# Revit family: Haworth_Cannot_Table
name_source: partatom
category: Furniture
revit_build: Autodesk Revit 2018 (Build: 20170223_1515(x64)
units: mm (PartAtom-declared; Revit-internal decimal feet)

## family parameters
Always vertical = Yes
Cut with Voids When Loaded = No
OmniClass Number = 23.40.20.00
OmniClass Title = General Furniture and Specialties
Room Calculation Point = No
Shared = No
Work Plane-Based = No

## types (1)
- HCCE-CNOT
    Actual Height = 1' - 6 3/4"
    Actual Radius = 0' - 11 13/32"
    Assembly Code = E2020200
    Base Finish = Haworth _ Metal _ Stainless Steel
    Description = Haworth Cannot Table
    Manufacturer = Haworth
    Model = HCCE-CNOT
    Post Spacing = 0' - 11 7/32"
    Revision = 4
    Size = Verify Final Dim. w/ Haworth
    Standard Depth = 23 inches
    Standard Heights = 18.75 inches
    Standard Width = 23 inches
    Top Radius = 0' - 11 1/32"
    URL = http://www.haworth.com
    URL - Product = https://www.haworth.com
    Warranty = http://www.haworth.com

## geometry (parser evidence)
native form markers: Sweep x2
no freeform markers — native parametric forms only
